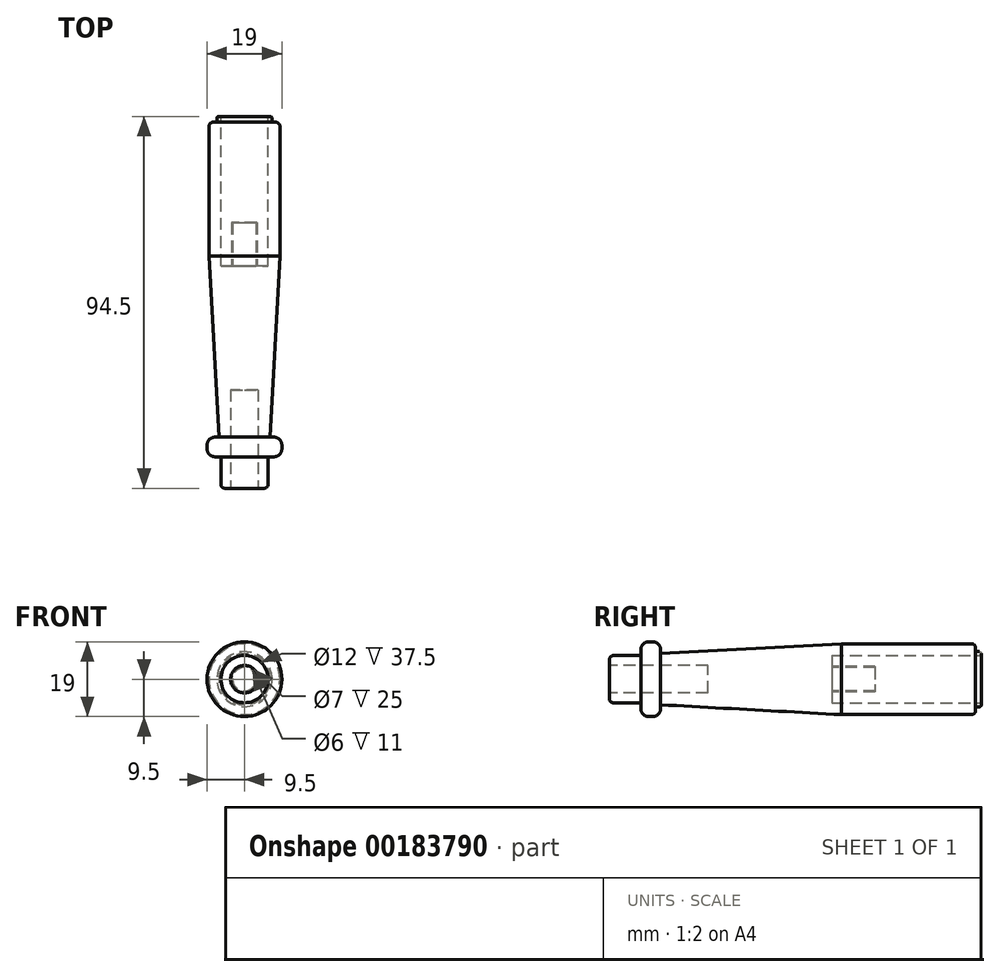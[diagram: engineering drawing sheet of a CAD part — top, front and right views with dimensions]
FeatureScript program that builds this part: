
annotation { "Feature Type Name" : "Feature", "Feature Type Description" : "" }
export const myFeature = defineFeature(function(context is Context, id is Id, definition is map)
    precondition{}
    {
        {
            var Q0;
            Q0=qCreatedBy(makeId("Front.planeOp"),FACE);
            var sketch = newSketch(context, id + "F0", { "sketchPlane" : qUnion([Q0])});
            skCircle(sketch, "E0", {"center": v(0, 0) * mm, "radius": 9 * mm});
            skSolve(sketch);
        }
        {
            var Q0;
            Q0 = qSketchRegion(id + "F0", true);
            extrude(context, id + "F1", {"entities" : qUnion([Q0]), "depth" : 34 * mm});
        }
        {
            var Q0;
            Q0=makeQuery(id+"F1.opExtrude","CAP_FACE",FACE,{"disambiguationData":[OSD([sQuery(id+"F0.wireOp",EDGE,"E0")])],"isStart":false});
            var sketch = newSketch(context, id + "F2", { "sketchPlane" : qUnion([Q0])});
            skCircle(sketch, "E1", {"center": v(0, 0) * mm, "radius": 9 * mm});
            skSolve(sketch);
        }
        {
            var Q0;
            Q0=qCreatedBy(makeId("Front.planeOp"),FACE);
            cPlane(context, id + "F3", {"entities" : qUnion([Q0]), "cplaneType" : CPlaneType.OFFSET, "offset" : 80 * mm, "width" : 150 * mm, "height" : 150 * mm});
        }
        {
            var Q0;
            Q0=qCreatedBy(id+"F3.planeOp",FACE);
            var sketch = newSketch(context, id + "F4", { "sketchPlane" : qUnion([Q0])});
            skCircle(sketch, "E2", {"center": v(0, 0) * mm, "radius": 6.5 * mm});
            skSolve(sketch);
        }
        {
            var Q1;
            Q1=makeQuery(id+"F2.imprint","IMPRINT",FACE,{"disambiguationData":[TD([[makeQuery(id+"F2.imprint","IMPRINT",EDGE,{"derivedFrom":sQuery(id+"F2.wireOp",EDGE,"E1")}),1.0]])]});
            var Q2;
            Q2=makeQuery(id+"F4.imprint","IMPRINT",FACE,{"disambiguationData":[TD([[makeQuery(id+"F4.imprint","IMPRINT",EDGE,{"derivedFrom":sQuery(id+"F4.wireOp",EDGE,"E2")}),1.0]])]});
            loft(context, id + "F5", {"operationType" : NewBodyOperationType.ADD, "sheetProfilesArray" : [{ "sheetProfileEntities" : qUnion([Q1]) }, { "sheetProfileEntities" : qUnion([Q2]) }]});
        }
        {
            var Q0;
            Q0=makeQuery(id+"F5.opLoft","CAP_FACE",FACE,{"disambiguationData":[OSD([makeQuery(id+"F4.imprint","IMPRINT",FACE,{"disambiguationData":[TD([[makeQuery(id+"F4.imprint","IMPRINT",EDGE,{"derivedFrom":sQuery(id+"F4.wireOp",EDGE,"E2")}),1.0]])]})])],"isStart":true});
            var sketch = newSketch(context, id + "F6", { "sketchPlane" : qUnion([Q0])});
            skCircle(sketch, "E3", {"center": v(0, 0) * mm, "radius": 9.5 * mm});
            skSolve(sketch);
        }
        {
            var Q0;
            Q0 = qSketchRegion(id + "F6", true);
            extrude(context, id + "F7", {"entities" : qUnion([Q0]), "operationType" : NewBodyOperationType.ADD, "depth" : 5 * mm});
        }
        {
            var Q0;
            Q0=makeQuery(id+"F7.opExtrude","CAP_EDGE",EDGE,{"disambiguationData":[OSD([sQuery(id+"F6.wireOp",EDGE,"E3")])],"isStart":false});
            var Q1;
            Q1=makeQuery(id+"F7.opExtrude","CAP_EDGE",EDGE,{"disambiguationData":[OSD([sQuery(id+"F6.wireOp",EDGE,"E3")])],"isStart":true});
            fillet(context, id + "F8", {"entities" : qUnion([Q0, Q1]), "radius" : 2 * mm, "tangentPropagation" : true, "allowEdgeOverflow" : false});
        }
        {
            var Q0;
            Q0=makeQuery(id+"F7.opExtrude","CAP_FACE",FACE,{"disambiguationData":[OSD([sQuery(id+"F6.wireOp",EDGE,"E3")])],"isStart":false});
            var sketch = newSketch(context, id + "F9", { "sketchPlane" : qUnion([Q0])});
            skCircle(sketch, "E4", {"center": v(0, 0) * mm, "radius": 6 * mm});
            skSolve(sketch);
        }
        {
            var Q0;
            Q0 = qSketchRegion(id + "F9", true);
            extrude(context, id + "F10", {"entities" : qUnion([Q0]), "operationType" : NewBodyOperationType.ADD, "depth" : 8 * mm});
        }
        {
            var Q0;
            Q0=makeQuery(id+"F1.opExtrude","CAP_FACE",FACE,{"disambiguationData":[OSD([sQuery(id+"F0.wireOp",EDGE,"E0")])],"isStart":true});
            var sketch = newSketch(context, id + "F11", { "sketchPlane" : qUnion([Q0])});
            skCircle(sketch, "E5", {"center": v(0, 0) * mm, "radius": 6 * mm});
            skSolve(sketch);
        }
        {
            var Q0;
            Q0 = qSketchRegion(id + "F11", true);
            extrude(context, id + "F12", {"entities" : qUnion([Q0]), "operationType" : NewBodyOperationType.REMOVE, "oppositeDirection" : true, "depth" : 36.5 * mm});
        }
        {
            var Q0;
            Q0=makeQuery(id+"F1.opExtrude","CAP_FACE",FACE,{"disambiguationData":[OSD([sQuery(id+"F0.wireOp",EDGE,"E0")])],"isStart":true});
            var sketch = newSketch(context, id + "F13", { "sketchPlane" : qUnion([Q0])});
            skCircle(sketch, "E6", {"center": v(0, 0) * mm, "radius": 7 * mm});
            skSolve(sketch);
        }
        {
            var Q0;
            Q0=makeQuery(id+"F13.imprint","IMPRINT",FACE,{"disambiguationData":[TD([[makeQuery(id+"F13.imprint","IMPRINT",EDGE,{"derivedFrom":sQuery(id+"F13.wireOp",EDGE,"E6")}),1.0]])]});
            extrude(context, id + "F14", {"entities" : qUnion([Q0]), "operationType" : NewBodyOperationType.ADD, "depth" : 1.5 * mm});
        }
        {
            var Q0;
            Q0=makeQuery(id+"F1.opExtrude","CAP_EDGE",EDGE,{"disambiguationData":[OSD([sQuery(id+"F0.wireOp",EDGE,"E0")])],"isStart":true});
            fillet(context, id + "F15", {"entities" : qUnion([Q0]), "radius" : 1 * mm, "tangentPropagation" : true, "allowEdgeOverflow" : false});
        }
        {
            var Q0;
            Q0=makeQuery(id+"F14.opExtrude","CAP_EDGE",EDGE,{"disambiguationData":[OSD([sQuery(id+"F11.wireOp",EDGE,"E5")])],"isStart":false});
            var Q1;
            Q1=makeQuery(id+"F14.opExtrude","CAP_EDGE",EDGE,{"disambiguationData":[OSD([sQuery(id+"F13.wireOp",EDGE,"E6")])],"isStart":false});
            fillet(context, id + "F16", {"entities" : qUnion([Q0, Q1]), "radius" : 0.5 * mm, "tangentPropagation" : true, "allowEdgeOverflow" : false});
        }
        {
            var Q0;
            Q0=makeQuery(id+"F10.opExtrude","CAP_FACE",FACE,{"disambiguationData":[OSD([sQuery(id+"F9.wireOp",EDGE,"E4")])],"isStart":false});
            var sketch = newSketch(context, id + "F17", { "sketchPlane" : qUnion([Q0])});
            skCircle(sketch, "E7", {"center": v(0, 0) * mm, "radius": 3.5 * mm});
            skSolve(sketch);
        }
        {
            var Q0;
            Q0 = qSketchRegion(id + "F17", true);
            extrude(context, id + "F18", {"entities" : qUnion([Q0]), "operationType" : NewBodyOperationType.REMOVE, "oppositeDirection" : true, "depth" : 25 * mm});
        }
        {
            var Q0;
            Q0=makeQuery(id+"F10.opExtrude","CAP_EDGE",EDGE,{"disambiguationData":[OSD([sQuery(id+"F9.wireOp",EDGE,"E4")])],"isStart":false});
            fillet(context, id + "F19", {"entities" : qUnion([Q0]), "radius" : 1 * mm, "tangentPropagation" : true, "allowEdgeOverflow" : false});
        }
        {
            var Q0;
            Q0=makeQuery(id+"F12.boolean.opBoolean","COPY",FACE,{"derivedFrom":makeQuery(id+"F12.opExtrude","CAP_FACE",FACE,{"disambiguationData":[OSD([sQuery(id+"F11.wireOp",EDGE,"E5")])],"isStart":false})});
            var sketch = newSketch(context, id + "F20", { "sketchPlane" : qUnion([Q0])});
            skCircle(sketch, "E8", {"center": v(0, 0) * mm, "radius": 3 * mm});
            skCircle(sketch, "E9", {"center": v(0, 0) * mm, "radius": 3.25 * mm});
            skSolve(sketch);
        }
        {
            var Q0;
            Q0=makeQuery(id+"F20.imprint","IMPRINT",FACE,{"disambiguationData":[TD([[makeQuery(id+"F20.imprint","IMPRINT",EDGE,{"derivedFrom":sQuery(id+"F20.wireOp",EDGE,"E8")}),-1.0]])]});
            extrude(context, id + "F21", {"entities" : qUnion([Q0]), "operationType" : NewBodyOperationType.ADD, "depth" : 11 * mm});
        }
    });
